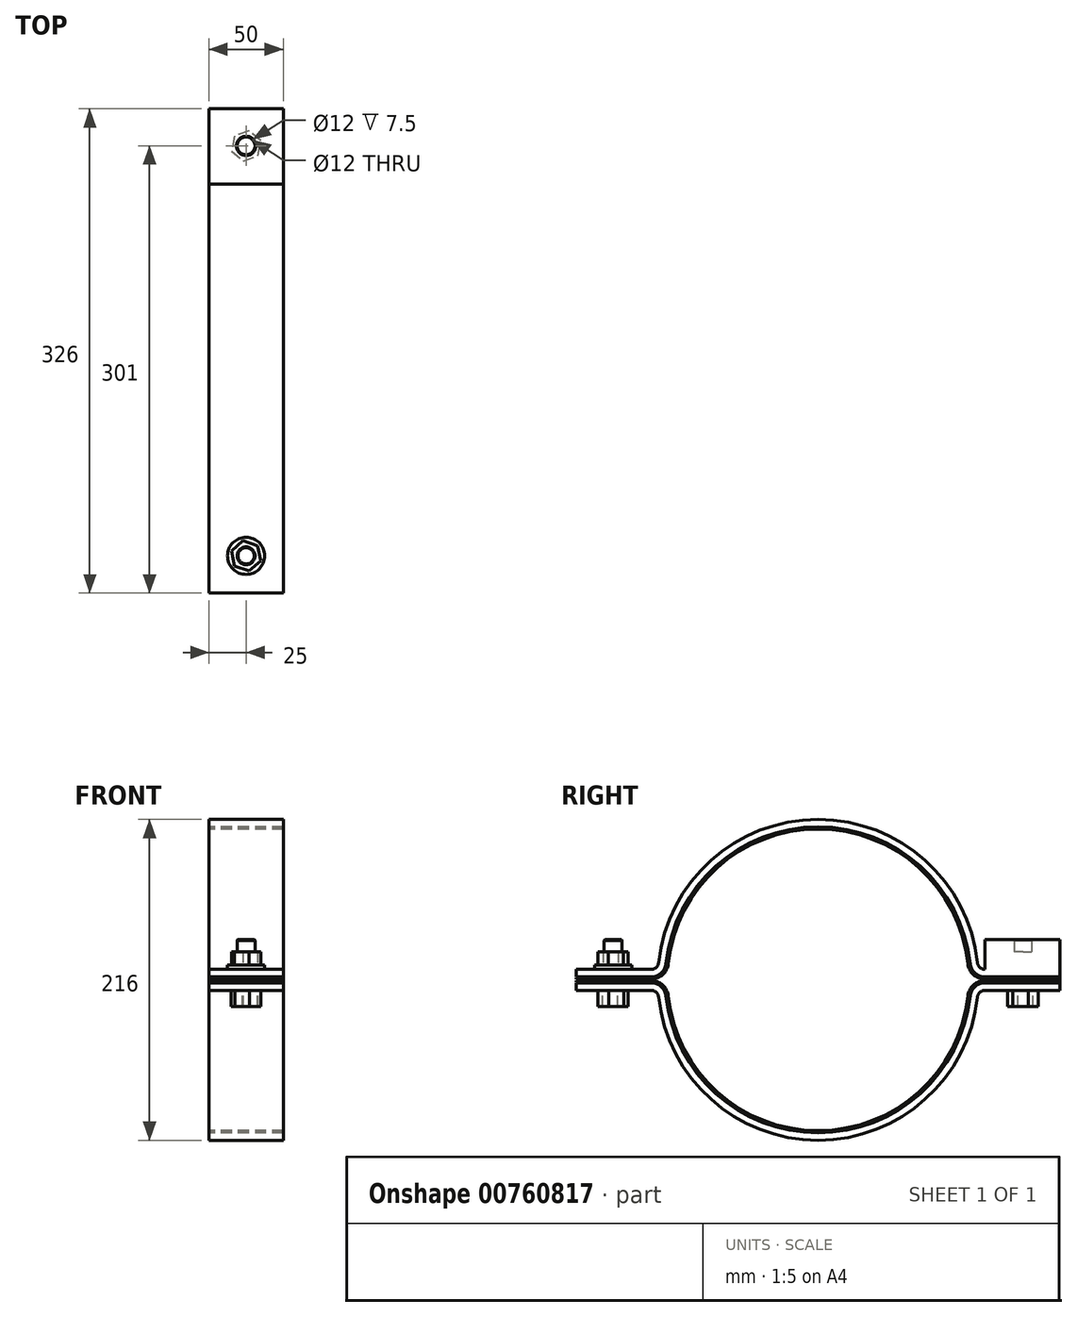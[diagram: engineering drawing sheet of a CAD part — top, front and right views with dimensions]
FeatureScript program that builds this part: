
annotation { "Feature Type Name" : "Feature", "Feature Type Description" : "" }
export const myFeature = defineFeature(function(context is Context, id is Id, definition is map)
    precondition{}
    {
        {
            var Q0;
            Q0=qCreatedBy(makeId("Right.planeOp"),FACE);
            var sketch = newSketch(context, id + "F0", { "sketchPlane" : qUnion([Q0])});
            skArc(sketch, "E0", {"start": v(-107.39, -11.47) * mm, "mid": v(0, -108) * mm, "end": v(107.39, -11.47) * mm});
            skArc(sketch, "E1.0", {"start": v(-102.42, -10.94) * mm, "mid": v(0, -103) * mm, "end": v(102.42, -10.94) * mm});
            skLineSegment(sketch, "E2", {"start": v(-108, 0) * mm, "end": v(108, 0) * mm});
            skLineSegment(sketch, "E3", {"start": v(163, 7) * mm, "end": v(112.36, 7) * mm});
            skLineSegment(sketch, "E4", {"start": v(163, -7) * mm, "end": v(112.36, -7) * mm});
            skLineSegment(sketch, "E5.0", {"start": v(163, -2) * mm, "end": v(112.36, -2) * mm});
            skLineSegment(sketch, "E6.0", {"start": v(163, 2) * mm, "end": v(112.36, 2) * mm});
            skLineSegment(sketch, "E7", {"start": v(163, 7) * mm, "end": v(163, 2) * mm});
            skLineSegment(sketch, "E8", {"start": v(163, -2) * mm, "end": v(163, -7) * mm});
            skLineSegment(sketch, "E9", {"start": v(-163, -2) * mm, "end": v(-163, -7) * mm});
            skLineSegment(sketch, "E10", {"start": v(-163, 7) * mm, "end": v(-163, 2) * mm});
            skLineSegment(sketch, "E11.trimOffspring", {"start": v(-112.36, 7) * mm, "end": v(-163, 7) * mm});
            skLineSegment(sketch, "E12.trimOffspring", {"start": v(-112.36, 2) * mm, "end": v(-163, 2) * mm});
            skLineSegment(sketch, "E13.trimOffspring", {"start": v(-112.36, -2) * mm, "end": v(-163, -2) * mm});
            skLineSegment(sketch, "E14.trimOffspring", {"start": v(-112.36, -7) * mm, "end": v(-163, -7) * mm});
            skArc(sketch, "E15.trimOffspring", {"start": v(102.42, 10.94) * mm, "mid": v(0, 103) * mm, "end": v(-102.42, 10.94) * mm});
            skArc(sketch, "E16.trimOffspring", {"start": v(107.39, 11.47) * mm, "mid": v(0, 108) * mm, "end": v(-107.39, 11.47) * mm});
            skPoint(sketch, "E17.visualSharp", {"position": v(102.98, 2) * mm});
            skArc(sketch, "E17.filletArc", {"start": v(102.42, 10.94) * mm, "mid": v(105.68, 4.56) * mm, "end": v(112.36, 2) * mm});
            skPoint(sketch, "E18.visualSharp", {"position": v(107.77, 7) * mm});
            skArc(sketch, "E18.filletArc", {"start": v(107.39, 11.47) * mm, "mid": v(109.02, 8.28) * mm, "end": v(112.36, 7) * mm});
            skPoint(sketch, "E19.visualSharp", {"position": v(102.98, -2) * mm});
            skArc(sketch, "E19.filletArc", {"start": v(112.36, -2) * mm, "mid": v(105.68, -4.56) * mm, "end": v(102.42, -10.94) * mm});
            skPoint(sketch, "E20.visualSharp", {"position": v(-102.98, 2) * mm});
            skArc(sketch, "E20.filletArc", {"start": v(-112.36, 2) * mm, "mid": v(-105.68, 4.56) * mm, "end": v(-102.42, 10.94) * mm});
            skPoint(sketch, "E21.visualSharp", {"position": v(-102.98, -2) * mm});
            skArc(sketch, "E21.filletArc", {"start": v(-102.42, -10.94) * mm, "mid": v(-105.68, -4.56) * mm, "end": v(-112.36, -2) * mm});
            skPoint(sketch, "E22.visualSharp", {"position": v(107.77, -7) * mm});
            skArc(sketch, "E22.filletArc", {"start": v(112.36, -7) * mm, "mid": v(109.02, -8.28) * mm, "end": v(107.39, -11.47) * mm});
            skPoint(sketch, "E23.visualSharp", {"position": v(-107.77, 7) * mm});
            skArc(sketch, "E23.filletArc", {"start": v(-112.36, 7) * mm, "mid": v(-109.02, 8.28) * mm, "end": v(-107.39, 11.47) * mm});
            skPoint(sketch, "E24.visualSharp", {"position": v(-107.77, -7) * mm});
            skArc(sketch, "E24.filletArc", {"start": v(-107.39, -11.47) * mm, "mid": v(-109.02, -8.28) * mm, "end": v(-112.36, -7) * mm});
            skSolve(sketch);
        }
        {
            var Q0;
            Q0=makeQuery(id+"F0.imprint","IMPRINT",FACE,{"disambiguationData":[TD([[makeQuery(id+"F0.imprint","IMPRINT",EDGE,{"derivedFrom":sQuery(id+"F0.wireOp",EDGE,"E3")}),1.0]])]});
            var Q1;
            Q1=makeQuery(id+"F0.imprint","IMPRINT",FACE,{"disambiguationData":[TD([[makeQuery(id+"F0.imprint","IMPRINT",EDGE,{"derivedFrom":sQuery(id+"F0.wireOp",EDGE,"E0")}),1.0]])]});
            extrude(context, id + "F1", {"entities" : qUnion([Q0, Q1]), "endBound" : BoundingType.SYMMETRIC, "depth" : 50 * mm, "offsetDistance" : 25 * mm});
        }
        {
            var Q0;
            Q0=makeQuery(id+"F1.opExtrude","SWEPT_FACE",FACE,{"disambiguationData":[OSD([sQuery(id+"F0.wireOp",EDGE,"E3")])]});
            var sketch = newSketch(context, id + "F2", { "sketchPlane" : qUnion([Q0])});
            skCircle(sketch, "E25.cCircle", {"center": v(0, 138) * mm, "radius": 9 * mm, "construction": true});
            skLineSegment(sketch, "E25.0", {"start": v(-1.5, 127.72) * mm, "end": v(-9.66, 134.16) * mm});
            skLineSegment(sketch, "E25.1", {"start": v(-9.66, 134.16) * mm, "end": v(-8.15, 144.45) * mm});
            skLineSegment(sketch, "E25.2", {"start": v(-8.15, 144.45) * mm, "end": v(1.5, 148.28) * mm});
            skLineSegment(sketch, "E25.3", {"start": v(1.5, 148.28) * mm, "end": v(9.66, 141.84) * mm});
            skLineSegment(sketch, "E25.4", {"start": v(9.66, 141.84) * mm, "end": v(8.15, 131.55) * mm});
            skLineSegment(sketch, "E25.5", {"start": v(8.15, 131.55) * mm, "end": v(-1.5, 127.72) * mm});
            skPoint(sketch, "E25.0.midPoint", {"position": v(-5.58, 130.94) * mm});
            skCircle(sketch, "E26", {"center": v(0, 138) * mm, "radius": 6 * mm});
            skCircle(sketch, "E27.cCircle", {"center": v(0, -138) * mm, "radius": 9 * mm, "construction": true});
            skLineSegment(sketch, "E27.0", {"start": v(-7.77, -144.9) * mm, "end": v(-9.86, -134.72) * mm});
            skLineSegment(sketch, "E27.1", {"start": v(-9.86, -134.72) * mm, "end": v(-2.09, -127.82) * mm});
            skLineSegment(sketch, "E27.2", {"start": v(-2.09, -127.82) * mm, "end": v(7.77, -131.1) * mm});
            skLineSegment(sketch, "E27.3", {"start": v(7.77, -131.1) * mm, "end": v(9.86, -141.28) * mm});
            skLineSegment(sketch, "E27.4", {"start": v(9.86, -141.28) * mm, "end": v(2.09, -148.18) * mm});
            skLineSegment(sketch, "E27.5", {"start": v(2.09, -148.18) * mm, "end": v(-7.77, -144.9) * mm});
            skPoint(sketch, "E27.0.midPoint", {"position": v(-8.82, -139.8) * mm});
            skCircle(sketch, "E28", {"center": v(0, 138) * mm, "radius": 12.5 * mm});
            skCircle(sketch, "E29", {"center": v(0, -138) * mm, "radius": 12.5 * mm});
            skCircle(sketch, "E30", {"center": v(0, -138) * mm, "radius": 6 * mm});
            skSolve(sketch);
        }
        {
            var Q0;
            Q0=makeQuery(id+"F2.imprint","IMPRINT",FACE,{"disambiguationData":[TD([[makeQuery(id+"F2.imprint","IMPRINT",EDGE,{"derivedFrom":sQuery(id+"F2.wireOp",EDGE,"E27.0")}),-1.0]])]});
            var Q1;
            Q1=makeQuery(id+"F2.imprint","IMPRINT",FACE,{"disambiguationData":[TD([[makeQuery(id+"F2.imprint","IMPRINT",EDGE,{"derivedFrom":sQuery(id+"F2.wireOp",EDGE,"E25.0")}),-1.0]])]});
            var Q2;
            Q2=makeQuery(id+"F2.imprint","IMPRINT",FACE,{"disambiguationData":[TD([[makeQuery(id+"F2.imprint","IMPRINT",EDGE,{"derivedFrom":sQuery(id+"F2.wireOp",EDGE,"E26")}),1.0]])]});
            extrude(context, id + "F3", {"entities" : qUnion([Q0, Q1, Q2]), "operationType" : NewBodyOperationType.ADD, "depth" : 12 * mm, "offsetDistance" : 25 * mm});
        }
        {
            var Q0;
            Q0=makeQuery(id+"F2.imprint","IMPRINT",FACE,{"disambiguationData":[TD([[makeQuery(id+"F2.imprint","IMPRINT",EDGE,{"derivedFrom":sQuery(id+"F2.wireOp",EDGE,"E27.0")}),1.0]])]});
            var Q1;
            Q1=makeQuery(id+"F2.imprint","IMPRINT",FACE,{"disambiguationData":[TD([[makeQuery(id+"F2.imprint","IMPRINT",EDGE,{"derivedFrom":sQuery(id+"F2.wireOp",EDGE,"E25.0")}),1.0]])]});
            extrude(context, id + "F4", {"entities" : qUnion([Q0, Q1]), "operationType" : NewBodyOperationType.ADD, "depth" : 3 * mm, "offsetDistance" : 25 * mm});
        }
        {
            var Q0;
            Q0=makeQuery(id+"F1.opExtrude","SWEPT_FACE",FACE,{"disambiguationData":[OSD([sQuery(id+"F0.wireOp",EDGE,"E6.0")])]});
            var sketch = newSketch(context, id + "F5", { "sketchPlane" : qUnion([Q0])});
            skCircle(sketch, "E31.0", {"center": v(0, -138) * mm, "radius": 6 * mm});
            skPoint(sketch, "E32.0", {"position": v(0, 138) * mm});
            skCircle(sketch, "E33", {"center": v(0, 138) * mm, "radius": 6 * mm});
            skSolve(sketch);
        }
        {
            var Q0;
            Q0=makeQuery(id+"F5.imprint","IMPRINT",FACE,{"disambiguationData":[TD([[makeQuery(id+"F5.imprint","IMPRINT",EDGE,{"derivedFrom":sQuery(id+"F5.wireOp",EDGE,"E31.0")}),-1.0]])]});
            var Q1;
            Q1=makeQuery(id+"F5.imprint","IMPRINT",FACE,{"disambiguationData":[TD([[makeQuery(id+"F5.imprint","IMPRINT",EDGE,{"derivedFrom":sQuery(id+"F5.wireOp",EDGE,"E33")}),1.0]])]});
            extrude(context, id + "F6", {"entities" : qUnion([Q0, Q1]), "operationType" : NewBodyOperationType.ADD, "oppositeDirection" : true, "depth" : 25 * mm, "offsetDistance" : 25 * mm});
        }
        {
            var Q0;
            Q0=makeQuery(id+"F1.opExtrude","SWEPT_FACE",FACE,{"disambiguationData":[OSD([sQuery(id+"F0.wireOp",EDGE,"E14.trimOffspring")])]});
            var sketch = newSketch(context, id + "F7", { "sketchPlane" : qUnion([Q0])});
            skCircle(sketch, "E34.0", {"center": v(0, 138) * mm, "radius": 6 * mm});
            skCircle(sketch, "E35.0.0", {"center": v(0, -138) * mm, "radius": 6 * mm});
            skCircle(sketch, "E36.cCircle", {"center": v(0, 138) * mm, "radius": 9 * mm, "construction": true});
            skLineSegment(sketch, "E36.0", {"start": v(-2.35, 127.88) * mm, "end": v(-9.94, 134.98) * mm});
            skLineSegment(sketch, "E36.1", {"start": v(-9.94, 134.98) * mm, "end": v(-7.59, 145.1) * mm});
            skLineSegment(sketch, "E36.2", {"start": v(-7.59, 145.1) * mm, "end": v(2.35, 148.12) * mm});
            skLineSegment(sketch, "E36.3", {"start": v(2.35, 148.12) * mm, "end": v(9.94, 141.02) * mm});
            skLineSegment(sketch, "E36.4", {"start": v(9.94, 141.02) * mm, "end": v(7.59, 130.9) * mm});
            skLineSegment(sketch, "E36.5", {"start": v(7.59, 130.9) * mm, "end": v(-2.35, 127.88) * mm});
            skPoint(sketch, "E36.0.midPoint", {"position": v(-6.15, 131.43) * mm});
            skCircle(sketch, "E37.cCircle", {"center": v(0, -138) * mm, "radius": 9 * mm, "construction": true});
            skLineSegment(sketch, "E37.0", {"start": v(7.9, -131.25) * mm, "end": v(9.8, -141.47) * mm});
            skLineSegment(sketch, "E37.1", {"start": v(9.8, -141.47) * mm, "end": v(1.9, -148.22) * mm});
            skLineSegment(sketch, "E37.2", {"start": v(1.9, -148.22) * mm, "end": v(-7.9, -144.75) * mm});
            skLineSegment(sketch, "E37.3", {"start": v(-7.9, -144.75) * mm, "end": v(-9.8, -134.53) * mm});
            skLineSegment(sketch, "E37.4", {"start": v(-9.8, -134.53) * mm, "end": v(-1.9, -127.78) * mm});
            skLineSegment(sketch, "E37.5", {"start": v(-1.9, -127.78) * mm, "end": v(7.9, -131.25) * mm});
            skPoint(sketch, "E37.0.midPoint", {"position": v(8.85, -136.36) * mm});
            skSolve(sketch);
        }
        {
            var Q0;
            Q0=makeQuery(id+"F7.imprint","IMPRINT",FACE,{"disambiguationData":[TD([[makeQuery(id+"F7.imprint","IMPRINT",EDGE,{"derivedFrom":sQuery(id+"F7.wireOp",EDGE,"E35.0.0")}),-1.0]])]});
            var Q1;
            Q1=makeQuery(id+"F7.imprint","IMPRINT",FACE,{"disambiguationData":[TD([[makeQuery(id+"F7.imprint","IMPRINT",EDGE,{"derivedFrom":sQuery(id+"F7.wireOp",EDGE,"E34.0")}),-1.0]])]});
            extrude(context, id + "F8", {"entities" : qUnion([Q0, Q1]), "operationType" : NewBodyOperationType.ADD, "depth" : 11 * mm, "offsetDistance" : 25 * mm});
        }
        {
            var Q0;
            Q0=makeQuery(id+"F8.boolean.opBoolean","SPLIT",FACE,{"disambiguationData":[TD([makeQuery(id+"F8.opExtrude","SWEPT_FACE",FACE,{"disambiguationData":[OSD([sQuery(id+"F7.wireOp",EDGE,"E34.0")])]})])],"derivedFrom":makeQuery(id+"F1.opExtrude","SWEPT_FACE",FACE,{"disambiguationData":[OSD([sQuery(id+"F0.wireOp",EDGE,"E14.trimOffspring")])]})});
            var Q1;
            Q1=makeQuery(id+"F8.boolean.opBoolean","SPLIT",FACE,{"disambiguationData":[TD([makeQuery(id+"F8.opExtrude","SWEPT_FACE",FACE,{"disambiguationData":[OSD([sQuery(id+"F7.wireOp",EDGE,"E35.0.0")])]})])],"derivedFrom":makeQuery(id+"F1.opExtrude","SWEPT_FACE",FACE,{"disambiguationData":[OSD([sQuery(id+"F0.wireOp",EDGE,"E4")])]})});
            var Q2;
            Q2=makeQuery(id+"F8.opExtrude","CAP_FACE",FACE,{"disambiguationData":[OSD([sQuery(id+"F7.wireOp",EDGE,"E35.0.0"),sQuery(id+"F7.wireOp",EDGE,"E37.0"),sQuery(id+"F7.wireOp",EDGE,"E37.1"),sQuery(id+"F7.wireOp",EDGE,"E37.2"),sQuery(id+"F7.wireOp",EDGE,"E37.3"),sQuery(id+"F7.wireOp",EDGE,"E37.4"),sQuery(id+"F7.wireOp",EDGE,"E37.5")])],"isStart":false});
            extrude(context, id + "F9", {"entities" : qUnion([Q0, Q1]), "operationType" : NewBodyOperationType.ADD, "endBound" : BoundingType.UP_TO_SURFACE, "depth" : 25 * mm, "endBoundEntityFace" : qUnion([Q2]), "offsetDistance" : 25 * mm});
        }
        {
            var Q0;
            Q0=makeQuery(id+"F1.opExtrude","SWEPT_FACE",FACE,{"disambiguationData":[OSD([sQuery(id+"F0.wireOp",EDGE,"E6.0")])]});
            var sketch = newSketch(context, id + "F10", { "sketchPlane" : qUnion([Q0])});
            skCircle(sketch, "E38.0", {"center": v(0, -138) * mm, "radius": 6 * mm});
            skCircle(sketch, "E39.0", {"center": v(0, 138) * mm, "radius": 6 * mm});
            skSolve(sketch);
        }
        {
            var Q0;
            Q0=makeQuery(id+"F10.imprint","IMPRINT",FACE,{"disambiguationData":[TD([[makeQuery(id+"F10.imprint","IMPRINT",EDGE,{"derivedFrom":sQuery(id+"F10.wireOp",EDGE,"E38.0")}),-1.0]])]});
            var Q1;
            Q1=makeQuery(id+"F10.imprint","IMPRINT",FACE,{"disambiguationData":[TD([[makeQuery(id+"F10.imprint","IMPRINT",EDGE,{"derivedFrom":sQuery(id+"F10.wireOp",EDGE,"E39.0")}),-1.0]])]});
            var Q2;
            Q2=makeQuery(id+"F1.opExtrude","SWEPT_FACE",FACE,{"disambiguationData":[OSD([sQuery(id+"F0.wireOp",EDGE,"E13.trimOffspring")])]});
            extrude(context, id + "F11", {"entities" : qUnion([Q0, Q1]), "endBound" : BoundingType.UP_TO_SURFACE, "depth" : 25 * mm, "endBoundEntityFace" : qUnion([Q2]), "offsetDistance" : 25 * mm});
        }
        {
            var Q0;
            Q0=makeQuery(id+"F1.opExtrude","CAP_FACE",FACE,{"disambiguationData":[OSD([sQuery(id+"F0.wireOp",EDGE,"E3"),sQuery(id+"F0.wireOp",EDGE,"E6.0"),sQuery(id+"F0.wireOp",EDGE,"E7"),sQuery(id+"F0.wireOp",EDGE,"E10"),sQuery(id+"F0.wireOp",EDGE,"E11.trimOffspring"),sQuery(id+"F0.wireOp",EDGE,"E12.trimOffspring"),sQuery(id+"F0.wireOp",EDGE,"E15.trimOffspring"),sQuery(id+"F0.wireOp",EDGE,"E16.trimOffspring"),sQuery(id+"F0.wireOp",EDGE,"E17.filletArc"),sQuery(id+"F0.wireOp",EDGE,"E18.filletArc"),sQuery(id+"F0.wireOp",EDGE,"E20.filletArc"),sQuery(id+"F0.wireOp",EDGE,"E23.filletArc")])],"isStart":true});
            var sketch = newSketch(context, id + "F12", { "sketchPlane" : qUnion([Q0])});
            skLineSegment(sketch, "E40.0", {"start": v(-163, 2) * mm, "end": v(-112.36, 2) * mm});
            skArc(sketch, "E41.0", {"start": v(-102.42, 10.94) * mm, "mid": v(-105.68, 4.56) * mm, "end": v(-112.36, 2) * mm});
            skArc(sketch, "E42.0", {"start": v(-102.42, 10.94) * mm, "mid": v(0, 103) * mm, "end": v(102.42, 10.94) * mm});
            skArc(sketch, "E43.0", {"start": v(112.36, 2) * mm, "mid": v(105.68, 4.56) * mm, "end": v(102.42, 10.94) * mm});
            skLineSegment(sketch, "E44.0", {"start": v(112.36, 2) * mm, "end": v(163, 2) * mm});
            skLineSegment(sketch, "E45.0", {"start": v(112.36, 1.5) * mm, "end": v(163, 1.5) * mm});
            skLineSegment(sketch, "E45.1", {"start": v(-163, 1.5) * mm, "end": v(-112.36, 1.5) * mm});
            skArc(sketch, "E45.2", {"start": v(-101.92, 10.88) * mm, "mid": v(-105.34, 4.2) * mm, "end": v(-112.36, 1.5) * mm});
            skArc(sketch, "E45.3", {"start": v(-101.92, 10.88) * mm, "mid": v(0, 102.5) * mm, "end": v(101.92, 10.88) * mm});
            skArc(sketch, "E45.4", {"start": v(112.36, 1.5) * mm, "mid": v(105.34, 4.2) * mm, "end": v(101.92, 10.88) * mm});
            skLineSegment(sketch, "E46.0", {"start": v(112.36, 0.5) * mm, "end": v(163, 0.5) * mm});
            skLineSegment(sketch, "E46.1", {"start": v(-163, 0.5) * mm, "end": v(-112.36, 0.5) * mm});
            skArc(sketch, "E46.2", {"start": v(-100.93, 10.78) * mm, "mid": v(-104.67, 3.45) * mm, "end": v(-112.36, 0.5) * mm});
            skArc(sketch, "E46.3", {"start": v(-100.93, 10.78) * mm, "mid": v(0, 101.5) * mm, "end": v(100.93, 10.78) * mm});
            skArc(sketch, "E46.4", {"start": v(112.36, 0.5) * mm, "mid": v(104.67, 3.45) * mm, "end": v(100.93, 10.78) * mm});
            skLineSegment(sketch, "E47", {"start": v(163, 1.5) * mm, "end": v(163, 0.5) * mm});
            skLineSegment(sketch, "E48", {"start": v(-163, 1.5) * mm, "end": v(-163, 0.5) * mm});
            skLineSegment(sketch, "E49.0", {"start": v(112.36, -2) * mm, "end": v(163, -2) * mm});
            skArc(sketch, "E50.0", {"start": v(102.42, -10.94) * mm, "mid": v(105.68, -4.56) * mm, "end": v(112.36, -2) * mm});
            skArc(sketch, "E51.0", {"start": v(102.42, -10.94) * mm, "mid": v(0, -103) * mm, "end": v(-102.42, -10.94) * mm});
            skArc(sketch, "E52.0", {"start": v(-112.36, -2) * mm, "mid": v(-105.68, -4.56) * mm, "end": v(-102.42, -10.94) * mm});
            skLineSegment(sketch, "E53.0", {"start": v(-163, -2) * mm, "end": v(-112.36, -2) * mm});
            skLineSegment(sketch, "E54.0", {"start": v(112.36, -1.5) * mm, "end": v(163, -1.5) * mm});
            skLineSegment(sketch, "E54.1", {"start": v(-163, -1.5) * mm, "end": v(-112.36, -1.5) * mm});
            skArc(sketch, "E54.2", {"start": v(-112.36, -1.5) * mm, "mid": v(-105.34, -4.2) * mm, "end": v(-101.92, -10.88) * mm});
            skArc(sketch, "E54.3", {"start": v(101.92, -10.88) * mm, "mid": v(0, -102.5) * mm, "end": v(-101.92, -10.88) * mm});
            skArc(sketch, "E54.4", {"start": v(101.92, -10.88) * mm, "mid": v(105.34, -4.2) * mm, "end": v(112.36, -1.5) * mm});
            skLineSegment(sketch, "E55.0", {"start": v(112.36, -0.5) * mm, "end": v(163, -0.5) * mm});
            skLineSegment(sketch, "E55.1", {"start": v(-163, -0.5) * mm, "end": v(-112.36, -0.5) * mm});
            skArc(sketch, "E55.2", {"start": v(-112.36, -0.5) * mm, "mid": v(-104.67, -3.45) * mm, "end": v(-100.93, -10.78) * mm});
            skArc(sketch, "E55.3", {"start": v(100.93, -10.78) * mm, "mid": v(0, -101.5) * mm, "end": v(-100.93, -10.78) * mm});
            skArc(sketch, "E55.4", {"start": v(100.93, -10.78) * mm, "mid": v(104.67, -3.45) * mm, "end": v(112.36, -0.5) * mm});
            skLineSegment(sketch, "E56", {"start": v(-163, -0.5) * mm, "end": v(-163, -1.5) * mm});
            skLineSegment(sketch, "E57", {"start": v(163, -0.5) * mm, "end": v(163, -1.5) * mm});
            skSolve(sketch);
        }
        {
            var Q0;
            Q0=makeQuery(id+"F12.imprint","IMPRINT",FACE,{"disambiguationData":[TD([[makeQuery(id+"F12.imprint","IMPRINT",EDGE,{"derivedFrom":sQuery(id+"F12.wireOp",EDGE,"E45.0")}),-1.0]])]});
            var Q1;
            Q1=makeQuery(id+"F12.imprint","IMPRINT",FACE,{"disambiguationData":[TD([[makeQuery(id+"F12.imprint","IMPRINT",EDGE,{"derivedFrom":sQuery(id+"F12.wireOp",EDGE,"E54.0")}),1.0]])]});
            var Q2;
            Q2=makeQuery(id+"F1.opExtrude","CAP_FACE",FACE,{"disambiguationData":[OSD([sQuery(id+"F0.wireOp",EDGE,"E0"),sQuery(id+"F0.wireOp",EDGE,"E1.0"),sQuery(id+"F0.wireOp",EDGE,"E4"),sQuery(id+"F0.wireOp",EDGE,"E5.0"),sQuery(id+"F0.wireOp",EDGE,"E8"),sQuery(id+"F0.wireOp",EDGE,"E9"),sQuery(id+"F0.wireOp",EDGE,"E13.trimOffspring"),sQuery(id+"F0.wireOp",EDGE,"E14.trimOffspring"),sQuery(id+"F0.wireOp",EDGE,"E19.filletArc"),sQuery(id+"F0.wireOp",EDGE,"E21.filletArc"),sQuery(id+"F0.wireOp",EDGE,"E22.filletArc"),sQuery(id+"F0.wireOp",EDGE,"E24.filletArc")])],"isStart":false});
            extrude(context, id + "F13", {"entities" : qUnion([Q0, Q1]), "endBound" : BoundingType.UP_TO_SURFACE, "oppositeDirection" : true, "depth" : 25 * mm, "endBoundEntityFace" : qUnion([Q2]), "offsetDistance" : 25 * mm});
        }
        {
            var Q0;
            Q0=makeQuery(id+"F6.opExtrude","CAP_EDGE",EDGE,{"disambiguationData":[OSD([sQuery(id+"F5.wireOp",EDGE,"E33")])],"isStart":false});
            var Q1;
            Q1=makeQuery(id+"F6.opExtrude","CAP_EDGE",EDGE,{"disambiguationData":[OSD([sQuery(id+"F5.wireOp",EDGE,"E31.0")])],"isStart":false});
            chamfer(context, id + "F14", {"entities" : qUnion([Q0, Q1]), "width" : 0.5 * mm, "tangentPropagation" : true});
        }
    });
